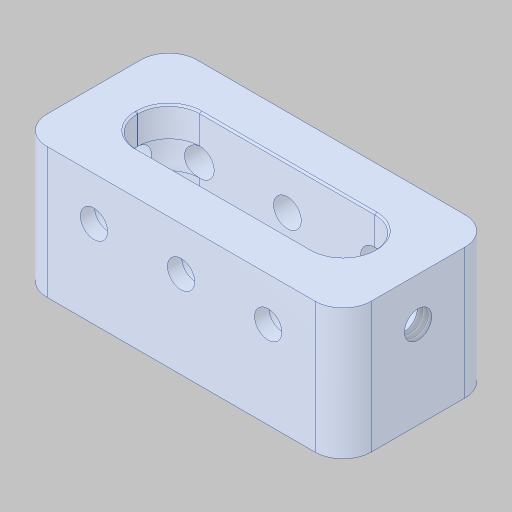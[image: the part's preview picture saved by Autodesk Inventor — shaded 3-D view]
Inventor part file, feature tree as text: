
AUTODESK INVENTOR PART (.ipt)
format: ipt  version: 2023.5 (Build 275446000, 446)  size: 352,256 bytes
history: native  units: in
note: dims shown in document units (in); Inventor stores cm internally (conversion verified against a paired STEP export)
features: sketch x4, hole x3, projected_geometry x2, extrude x1, chamfer x1
ambient origin geometry x8: Origin, YZ Plane, XZ Plane, XY Plane, X Axis, Y Axis, Z Axis, Center Point
bodies: Solid1 (feature_tree)
feature tree (11):
  extrude  "Extrusion1"  Depth=1.0in TaperAngle=0.0deg
  hole  "Hole1"  [1 undecoded]
  hole  "Hole2"  [1 undecoded]
  hole  "Hole3"  [1 undecoded]
  sketch  "Sketch1"  dims[d0=0.0625in d1=1.0in d2=0.0in]
  projected_geometry  "Projected Loop1"
  sketch  "Sketch2"  dims[d3=0.156in d4=0.38in d5=0.385in d6=0.25in d7=0.563in d8=1.0in d9=0.8108in]
  projected_geometry  "Projected Loop2"
  sketch  "Sketch3"  dims[d10=0.196in d11=0.5in d12=0.375in d13=0.25in d14=0.5635in d15=1.0in d16=0.8108in]
  sketch  "Sketch4"  dims[d17=0.156in d18=0.38in d19=0.385in d20=0.25in d21=0.563in d22=1.0in d23=0.8108in]
  chamfer  "Chamfer2"  [1 undecoded]
note: 4 required parameter values undecoded (feature->parameter linkage not recoverable at this tier; creation-order binding heuristic only, values carry confidence <= 0.55)
